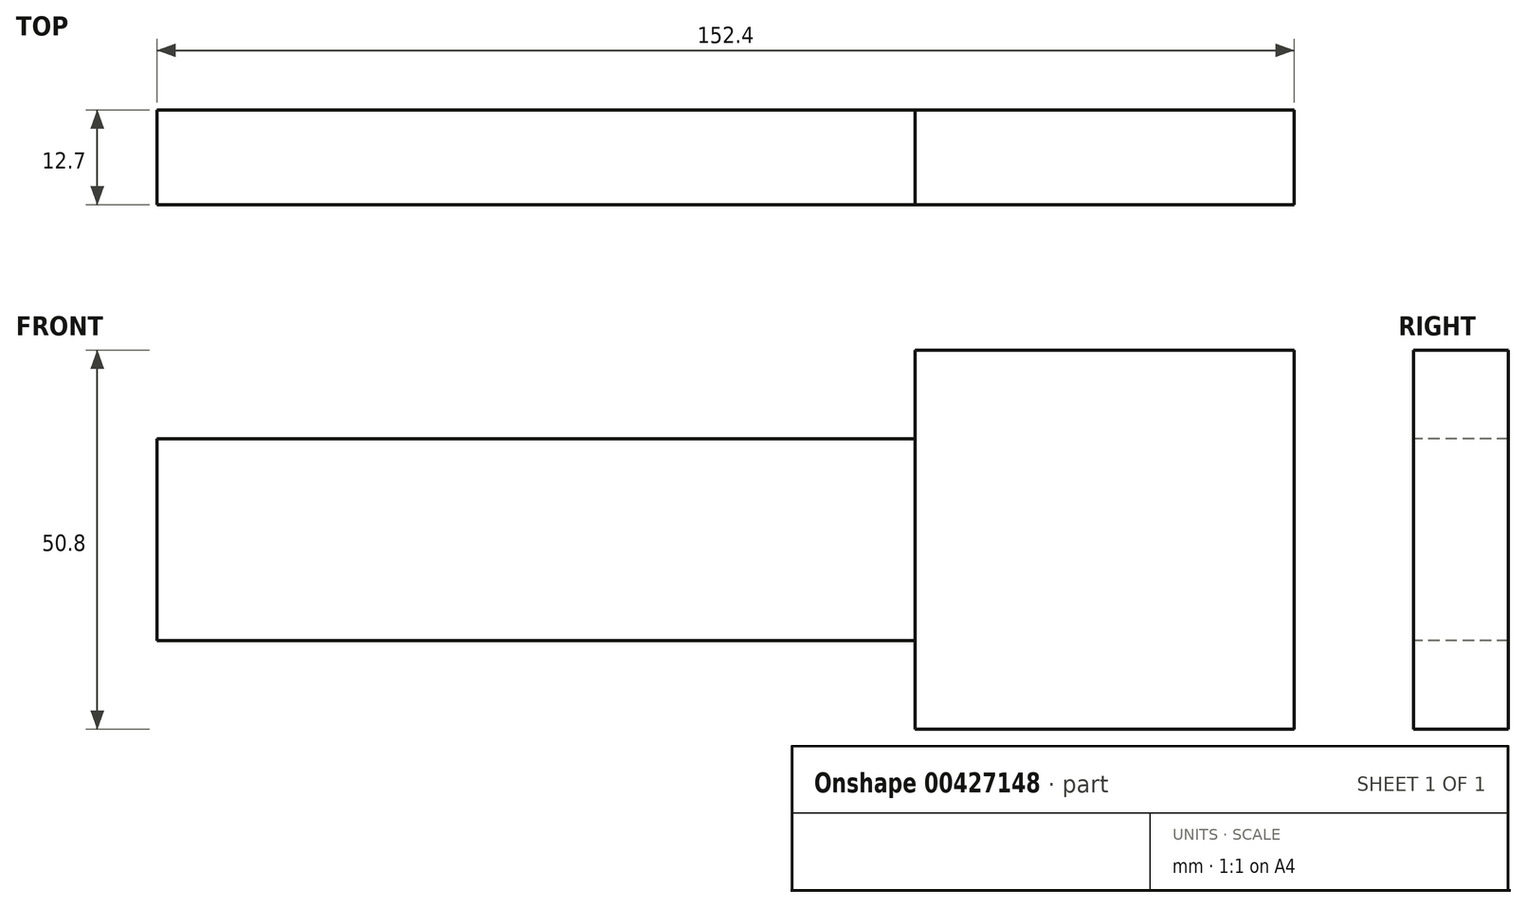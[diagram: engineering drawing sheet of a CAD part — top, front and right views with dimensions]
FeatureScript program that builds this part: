
annotation { "Feature Type Name" : "Feature", "Feature Type Description" : "" }
export const myFeature = defineFeature(function(context is Context, id is Id, definition is map)
    precondition{}
    {
        {
            var Q0;
            Q0=qCreatedBy(makeId("Front.planeOp"),FACE);
            var sketch = newSketch(context, id + "F0", { "sketchPlane" : qUnion([Q0])});
            skLineSegment(sketch, "E0.bottom", {"start": v(-25.4, 25.4) * mm, "end": v(25.4, 25.4) * mm});
            skLineSegment(sketch, "E0.top", {"start": v(-25.4, -25.4) * mm, "end": v(25.4, -25.4) * mm});
            skLineSegment(sketch, "E0.left", {"start": v(-25.4, 25.4) * mm, "end": v(-25.4, -25.4) * mm});
            skLineSegment(sketch, "E0.right", {"start": v(25.4, 25.4) * mm, "end": v(25.4, -25.4) * mm});
            skPoint(sketch, "E0.middle", {"position": v(0, 0) * mm});
            skSolve(sketch);
        }
        {
            var Q0;
            Q0 = qSketchRegion(id + "F0", true);
            extrude(context, id + "F1", {"entities" : qUnion([Q0]), "depth" : 12.7 * mm});
        }
        {
            var Q0;
            Q0=makeQuery(id+"F1.opExtrude","SWEPT_FACE",FACE,{"disambiguationData":[OSD([sQuery(id+"F0.wireOp",EDGE,"E0.left")])]});
            var sketch = newSketch(context, id + "F2", { "sketchPlane" : qUnion([Q0])});
            skLineSegment(sketch, "E1.top", {"start": v(0, 13.52) * mm, "end": v(12.7, 13.52) * mm});
            skLineSegment(sketch, "E1.left", {"start": v(0, 0) * mm, "end": v(0, 13.52) * mm});
            skLineSegment(sketch, "E1.right", {"start": v(12.7, 0) * mm, "end": v(12.7, 13.52) * mm});
            skLineSegment(sketch, "E2.top", {"start": v(0, -13.52) * mm, "end": v(12.7, -13.52) * mm});
            skLineSegment(sketch, "E2.left", {"start": v(0, 0) * mm, "end": v(0, -13.52) * mm});
            skLineSegment(sketch, "E2.right", {"start": v(12.7, 0) * mm, "end": v(12.7, -13.52) * mm});
            skSolve(sketch);
        }
        {
            var Q0;
            Q0 = qSketchRegion(id + "F2", true);
            extrude(context, id + "F3", {"entities" : qUnion([Q0]), "depth" : 101.6 * mm});
        }
    });
